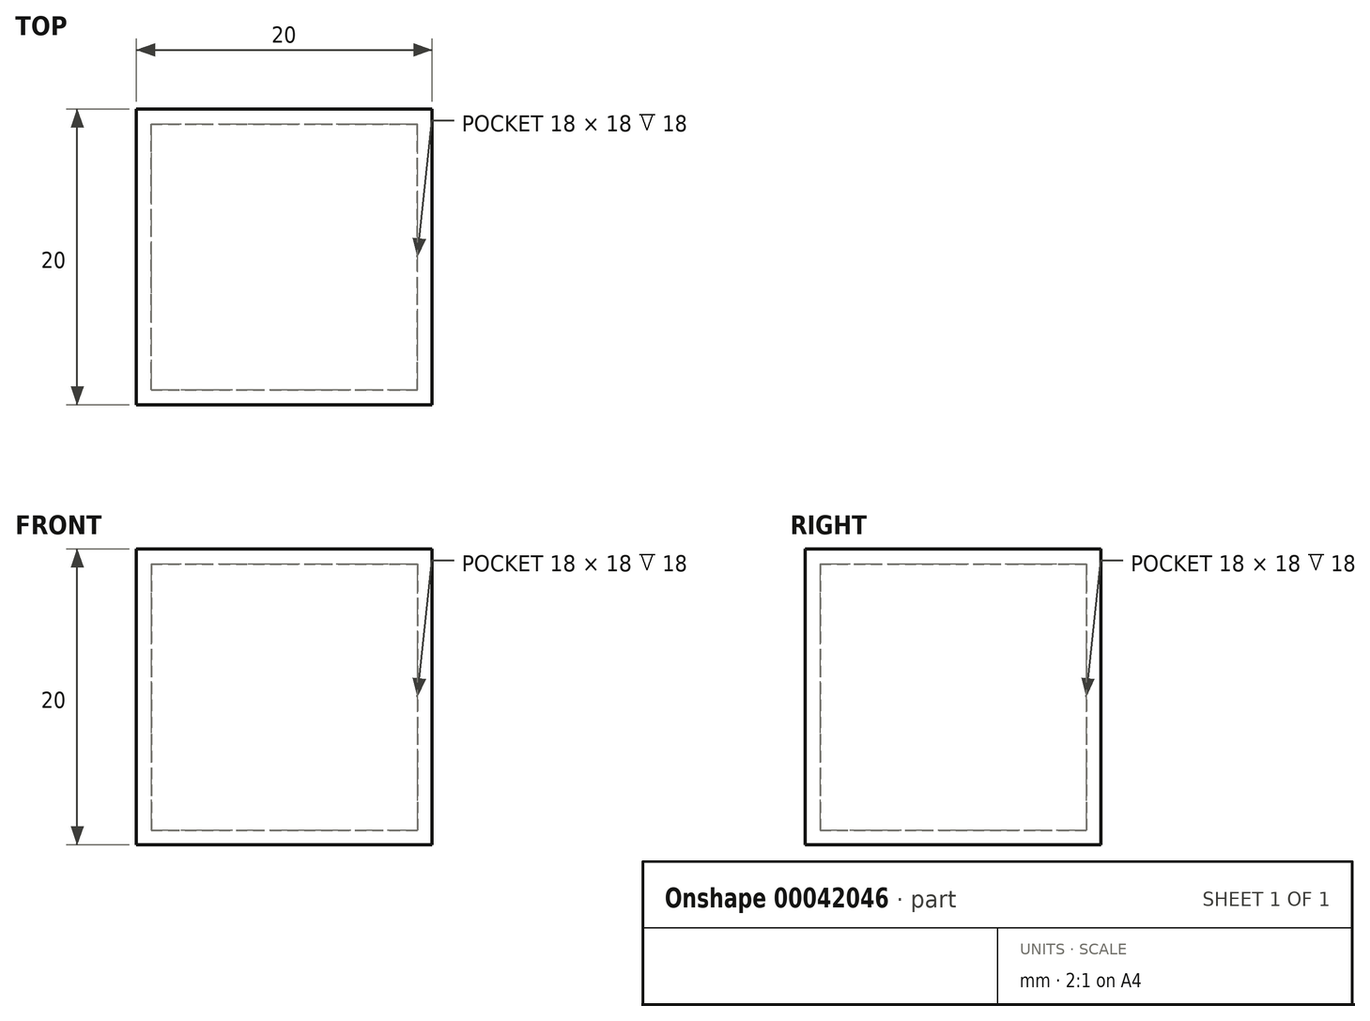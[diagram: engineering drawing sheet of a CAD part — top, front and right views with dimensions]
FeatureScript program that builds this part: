
annotation { "Feature Type Name" : "Feature", "Feature Type Description" : "" }
export const myFeature = defineFeature(function(context is Context, id is Id, definition is map)
    precondition{}
    {
        {
            var Q0;
            Q0=qCreatedBy(makeId("Front.planeOp"),FACE);
            var sketch = newSketch(context, id + "F0", { "sketchPlane" : qUnion([Q0])});
            skLineSegment(sketch, "E0.bottom", {"start": v(-10, 10) * mm, "end": v(10, 10) * mm});
            skLineSegment(sketch, "E0.top", {"start": v(-10, -10) * mm, "end": v(10, -10) * mm});
            skLineSegment(sketch, "E0.left", {"start": v(-10, 10) * mm, "end": v(-10, -10) * mm});
            skLineSegment(sketch, "E0.right", {"start": v(10, 10) * mm, "end": v(10, -10) * mm});
            skPoint(sketch, "E1", {"position": v(0, 10) * mm});
            skPoint(sketch, "E2", {"position": v(10, 0) * mm});
            skSolve(sketch);
        }
        {
            var Q0;
            Q0=qSketchRegion(id+"F0",true);
            extrude(context, id + "F1", {"entities" : qUnion([Q0]), "endBound" : BoundingType.SYMMETRIC, "depth" : 20 * mm});
        }
        {
            var Q0;
            Q0=makeQuery(id+"F1.opExtrude","SWEPT_FACE",FACE,{"disambiguationData":[OSD([sQuery(id+"F0.wireOp",EDGE,"E0.bottom")])]});
            var Q1;
            Q1=makeQuery(id+"F1.opExtrude","CAP_FACE",FACE,{"disambiguationData":[OSD([sQuery(id+"F0.wireOp",EDGE,"E0.bottom"),sQuery(id+"F0.wireOp",EDGE,"E0.top"),sQuery(id+"F0.wireOp",EDGE,"E0.left"),sQuery(id+"F0.wireOp",EDGE,"E0.right")])],"isStart":false});
            var Q2;
            Q2=makeQuery(id+"F1.opExtrude","SWEPT_FACE",FACE,{"disambiguationData":[OSD([sQuery(id+"F0.wireOp",EDGE,"E0.top")])]});
            var Q3;
            Q3=makeQuery(id+"F1.opExtrude","SWEPT_FACE",FACE,{"disambiguationData":[OSD([sQuery(id+"F0.wireOp",EDGE,"E0.left")])]});
            var Q4;
            Q4=makeQuery(id+"F1.opExtrude","SWEPT_FACE",FACE,{"disambiguationData":[OSD([sQuery(id+"F0.wireOp",EDGE,"E0.right")])]});
            var Q5;
            Q5=makeQuery(id+"F1.opExtrude","CAP_FACE",FACE,{"disambiguationData":[OSD([sQuery(id+"F0.wireOp",EDGE,"E0.bottom"),sQuery(id+"F0.wireOp",EDGE,"E0.top"),sQuery(id+"F0.wireOp",EDGE,"E0.left"),sQuery(id+"F0.wireOp",EDGE,"E0.right")])],"isStart":true});
            var Q6;
            Q6=makeQuery(id+"F1.opExtrude","SWEPT_BODY",BODY,{"disambiguationData":[OSD([sQuery(id+"F0.wireOp",EDGE,"E0.bottom"),sQuery(id+"F0.wireOp",EDGE,"E0.top"),sQuery(id+"F0.wireOp",EDGE,"E0.left"),sQuery(id+"F0.wireOp",EDGE,"E0.right")])]});
            shell(context, id + "F2", {"isHollow" : true, "entities" : qUnion([Q0, Q1, Q2, Q3, Q4, Q5]), "parts" : qUnion([Q6]), "thickness" : 1 * mm});
        }
    });
